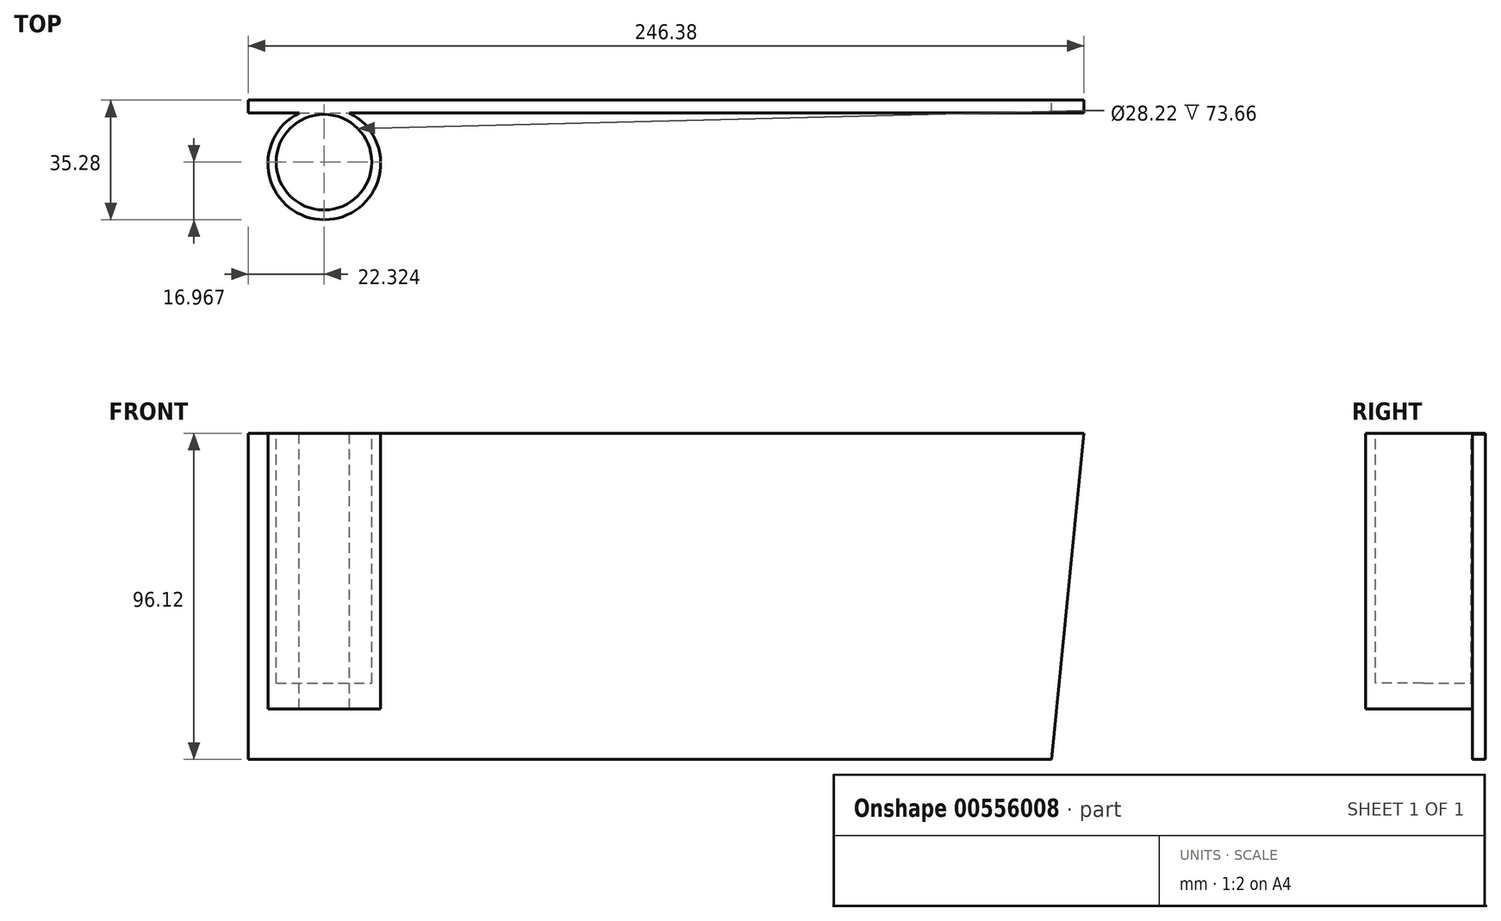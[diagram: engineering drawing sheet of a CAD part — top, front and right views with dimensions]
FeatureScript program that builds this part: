
annotation { "Feature Type Name" : "Feature", "Feature Type Description" : "" }
export const myFeature = defineFeature(function(context is Context, id is Id, definition is map)
    precondition{}
    {
        {
            var Q0;
            Q0=qCreatedBy(makeId("Front.planeOp"),FACE);
            var sketch = newSketch(context, id + "F0", { "sketchPlane" : qUnion([Q0])});
            skLineSegment(sketch, "E0.bottom", {"start": v(-123.2, 48.06) * mm, "end": v(123.2, 48.06) * mm});
            skLineSegment(sketch, "E0.top", {"start": v(-123.2, -48.06) * mm, "end": v(123.2, -48.06) * mm});
            skLineSegment(sketch, "E0.left", {"start": v(-123.2, 48.06) * mm, "end": v(-123.2, -48.06) * mm});
            skLineSegment(sketch, "E0.right", {"start": v(123.2, 48.06) * mm, "end": v(123.2, -48.06) * mm});
            skPoint(sketch, "E0.middle", {"position": v(0, 0) * mm});
            skSolve(sketch);
        }
        {
            var Q0;
            Q0=makeQuery(id+"F0.imprint","IMPRINT",FACE,{"disambiguationData":[TD([[makeQuery(id+"F0.imprint","IMPRINT",EDGE,{"derivedFrom":sQuery(id+"F0.wireOp",EDGE,"E0.bottom")}),-1.0]])]});
            extrude(context, id + "F1", {"entities" : qUnion([Q0]), "depth" : 3.8 * mm, "offsetDistance" : 25.4 * mm});
        }
        {
            var Q0;
            Q0=makeQuery(id+"F1.opExtrude","SWEPT_FACE",FACE,{"disambiguationData":[OSD([sQuery(id+"F0.wireOp",EDGE,"E0.bottom")])]});
            var sketch = newSketch(context, id + "F2", { "sketchPlane" : qUnion([Q0])});
            skCircle(sketch, "E1", {"center": v(-100.75, -18.67) * mm, "radius": 16.62 * mm});
            skCircle(sketch, "E2", {"center": v(-100.87, -18.31) * mm, "radius": 14.1 * mm});
            skSolve(sketch);
        }
        {
            var Q0;
            Q0=makeQuery(id+"F2.imprint","IMPRINT",FACE,{"disambiguationData":[TD([[makeQuery(id+"F2.imprint","IMPRINT",EDGE,{"derivedFrom":sQuery(id+"F2.wireOp",EDGE,"E2")}),-1.0]])]});
            var Q1;
            Q1=makeQuery(id+"FJSpL8YQpNJacnX_1.1.F2.imprint","IMPRINT",FACE,{"disambiguationData":[TD([[makeQuery(id+"FJSpL8YQpNJacnX_1.1.F2.imprint","IMPRINT",EDGE,{"derivedFrom":sQuery(id+"FJSpL8YQpNJacnX_1.1.F2.wireOp",EDGE,"E1")}),1.0]])]});
            extrude(context, id + "F3", {"entities" : qUnion([Q0, Q1]), "operationType" : NewBodyOperationType.ADD, "oppositeDirection" : true, "depth" : 81.28 * mm, "offsetDistance" : 25.4 * mm});
        }
        {
            var Q0;
            Q0=makeQuery(id+"F1.opExtrude","CAP_FACE",FACE,{"disambiguationData":[OSD([sQuery(id+"F0.wireOp",EDGE,"E0.bottom"),sQuery(id+"F0.wireOp",EDGE,"E0.top"),sQuery(id+"F0.wireOp",EDGE,"E0.left"),sQuery(id+"F0.wireOp",EDGE,"E0.right")])],"isStart":true});
            var sketch = newSketch(context, id + "F4", { "sketchPlane" : qUnion([Q0])});
            skLineSegment(sketch, "E3", {"start": v(-123.33, 49.57) * mm, "end": v(-113.04, -54.31) * mm});
            skLineSegment(sketch, "E4", {"start": v(-113.04, -54.31) * mm, "end": v(-128.9, -54.31) * mm});
            skLineSegment(sketch, "E5", {"start": v(-128.9, -54.31) * mm, "end": v(-123.09, 49.74) * mm});
            skSolve(sketch);
        }
        {
            var Q0;
            {var subQ0=sQuery(id+"F4.wireOp",EDGE,"E5");var subQ1=sQuery(id+"F4.wireOp",EDGE,"E3");var subQ2=makeQuery(id+"F4.imprint","INTERSECT",VERTEX,{"derivedFrom":[subQ1,subQ0]});Q0=makeQuery(id+"F4.imprint","IMPRINT",FACE,{"disambiguationData":[TD([[makeQuery(id+"F4.imprint","IMPRINT",EDGE,{"disambiguationData":[TD([[subQ2,-1.0]])],"derivedFrom":subQ1}),-1.0]])]});}
            extrude(context, id + "F5", {"entities" : qUnion([Q0]), "operationType" : NewBodyOperationType.REMOVE, "oppositeDirection" : true, "depth" : 25.4 * mm, "offsetDistance" : 25.4 * mm});
        }
        {
            var Q0;
            Q0=makeQuery(id+"F3.opExtrude","CAP_FACE",FACE,{"disambiguationData":[OSD([sQuery(id+"F0.wireOp",EDGE,"E0.bottom"),sQuery(id+"F2.wireOp",EDGE,"E1"),sQuery(id+"F2.wireOp",EDGE,"E2")])],"isStart":false});
            var sketch = newSketch(context, id + "F6", { "sketchPlane" : qUnion([Q0])});
            skCircle(sketch, "E6", {"center": v(-100.9, 18.22) * mm, "radius": 14.4 * mm});
            skSolve(sketch);
        }
        {
            var Q0;
            Q0=makeQuery(id+"F6.imprint","IMPRINT",FACE,{"disambiguationData":[TD([[makeQuery(id+"F6.imprint","IMPRINT",EDGE,{"derivedFrom":makeQuery(id+"F3.opExtrude","CAP_EDGE",EDGE,{"disambiguationData":[OSD([sQuery(id+"F2.wireOp",EDGE,"E2")])],"isStart":false})}),-1.0]])]});
            extrude(context, id + "F7", {"entities" : qUnion([Q0]), "operationType" : NewBodyOperationType.ADD, "oppositeDirection" : true, "depth" : 7.62 * mm, "offsetDistance" : 25.4 * mm});
        }
    });
